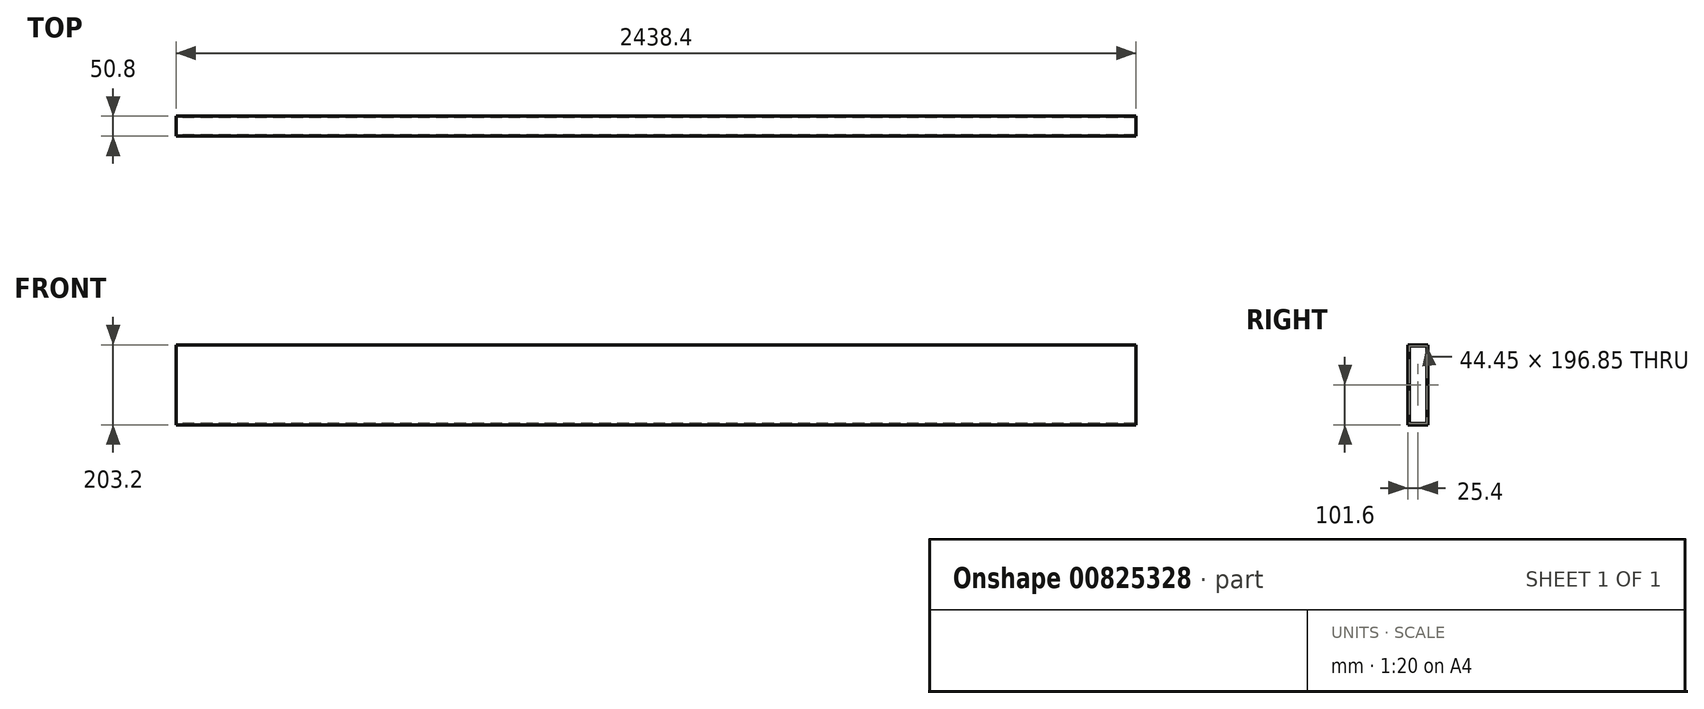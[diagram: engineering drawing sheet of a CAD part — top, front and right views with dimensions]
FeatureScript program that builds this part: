
annotation { "Feature Type Name" : "Feature", "Feature Type Description" : "" }
export const myFeature = defineFeature(function(context is Context, id is Id, definition is map)
    precondition{}
    {
        {
            var Q0;
            Q0=qCreatedBy(makeId("Right.planeOp"),FACE);
            var sketch = newSketch(context, id + "F0", { "sketchPlane" : qUnion([Q0])});
            skLineSegment(sketch, "E0.bottom", {"start": v(25.4, 1981.2) * mm, "end": v(-25.4, 1981.2) * mm});
            skLineSegment(sketch, "E0.top", {"start": v(25.4, 2184.4) * mm, "end": v(-25.4, 2184.4) * mm});
            skLineSegment(sketch, "E0.left", {"start": v(25.4, 1981.2) * mm, "end": v(25.4, 2184.4) * mm});
            skLineSegment(sketch, "E0.right", {"start": v(-25.4, 1981.2) * mm, "end": v(-25.4, 2184.4) * mm});
            skPoint(sketch, "E0.middle", {"position": v(0, 2082.8) * mm});
            skLineSegment(sketch, "E1", {"start": v(0, 2082.8) * mm, "end": v(0, 0) * mm, "construction": true});
            skLineSegment(sketch, "E2", {"start": v(0, 2082.8) * mm, "end": v(-558.08, 0) * mm, "construction": true});
            skLineSegment(sketch, "E3.0", {"start": v(-22.23, 1984.38) * mm, "end": v(-22.23, 2181.22) * mm});
            skLineSegment(sketch, "E3.1", {"start": v(22.22, 1984.38) * mm, "end": v(-22.23, 1984.38) * mm});
            skLineSegment(sketch, "E3.2", {"start": v(22.22, 1984.38) * mm, "end": v(22.22, 2181.22) * mm});
            skLineSegment(sketch, "E3.3", {"start": v(22.22, 2181.22) * mm, "end": v(-22.23, 2181.22) * mm});
            skSolve(sketch);
        }
        {
            var Q0;
            Q0 = qSketchRegion(id + "F0", true);
            extrude(context, id + "F1", {"entities" : qUnion([Q0]), "endBound" : BoundingType.SYMMETRIC, "depth" : 2438.4 * mm, "offsetDistance" : 25.4 * mm});
        }
    });
